# Revit family: _Шведская стенка+ турник+скамья для пресса+ турник для отжиманий
name_source: partatom
category: Антураж
revit_build: Autodesk Revit 2018 (Build: 20170927_1515(x64)
units: mm (PartAtom-declared; Revit-internal decimal feet)

## family parameters
Всегда вертикально = Да
Источник визуального образа = Геометрия семейства
На основе рабочей плоскости = Нет
Общий = Нет
При загрузке вырезать с полостями = Нет
Точка расчета площади = Нет

## types (1)
- Воркаут ЭКО-6 «Шведская стенка + турник + скамья для пресса + турник для отжиманий»
    URL = https://hobbyka.ru
    Артикул товара = Арт. 43402
    Высота = 2850 мм
    Группа модели = Спортивные площадки в ЭКО-стиле
    Длина = 3500 мм
    Изготовитель = ООО «Хоббика»
    Изображение типоразмера = Шведская стенка+ турник+скамья для пресса+ турник для отжиманий 001.png
    Материал изделия = Дерево, нержавеющая сталь, HPL
    Описание = Воркаут ЭКО-6 «Шведская стенка + турник + скамья для пресса + турник для отжиманий»
    Цвет каркаса = Орегон
    Ширина = 2900 мм
